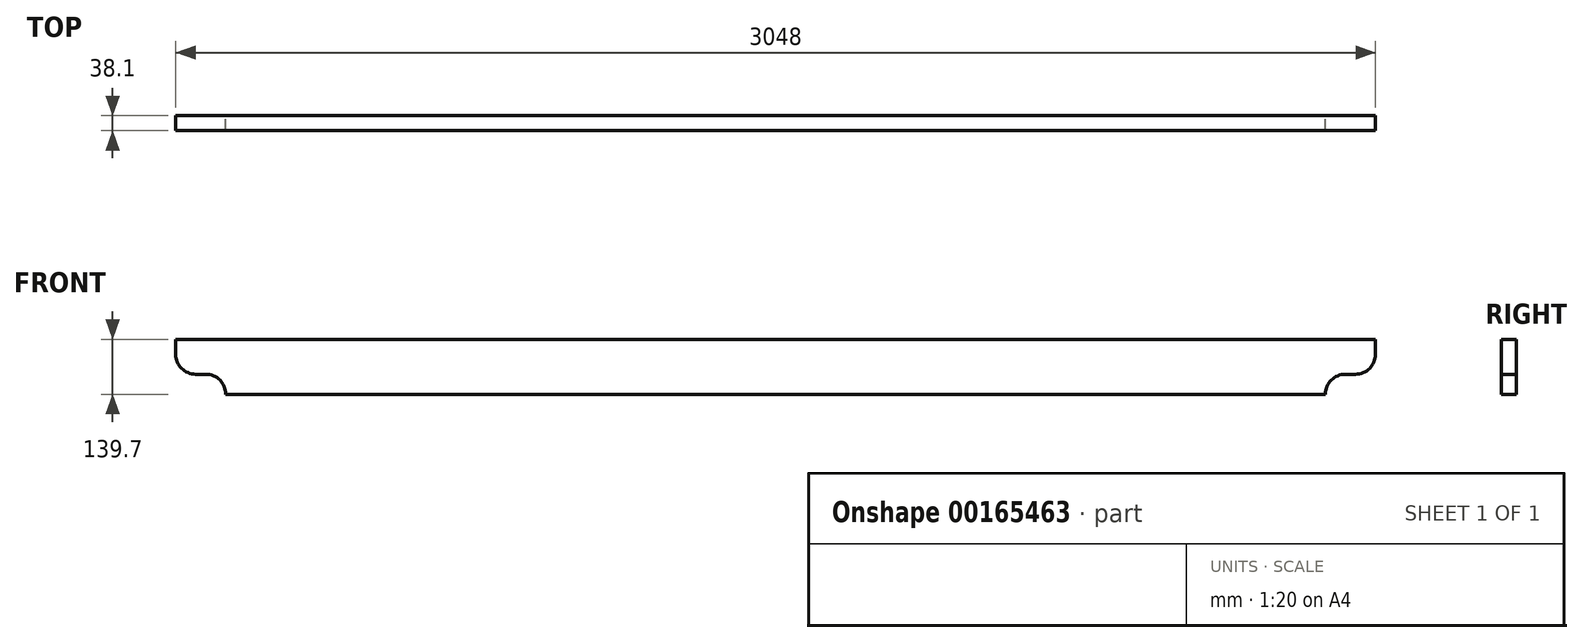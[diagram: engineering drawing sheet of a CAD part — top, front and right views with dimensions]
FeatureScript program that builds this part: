
annotation { "Feature Type Name" : "Feature", "Feature Type Description" : "" }
export const myFeature = defineFeature(function(context is Context, id is Id, definition is map)
    precondition{}
    {
        {
            var Q0;
            Q0=qCreatedBy(makeId("Front.planeOp"),FACE);
            var sketch = newSketch(context, id + "F0", { "sketchPlane" : qUnion([Q0])});
            skLineSegment(sketch, "E0.bottom", {"start": v(-1397, 0) * mm, "end": v(1397, 0) * mm});
            skLineSegment(sketch, "E0.top", {"start": v(-1524, 139.7) * mm, "end": v(1524, 139.7) * mm});
            skLineSegment(sketch, "E0.right", {"start": v(1524, 101.6) * mm, "end": v(1524, 139.7) * mm});
            skLineSegment(sketch, "E1", {"start": v(0, 0) * mm, "end": v(0, 139.7) * mm, "construction": true});
            skLineSegment(sketch, "E2", {"start": v(-1524, 139.7) * mm, "end": v(-1524, 101.6) * mm});
            skArc(sketch, "E3", {"start": v(-1524, 101.6) * mm, "mid": v(-1509.12, 65.68) * mm, "end": v(-1473.2, 50.8) * mm});
            skLineSegment(sketch, "E4", {"start": v(-1473.2, 50.8) * mm, "end": v(-1447.8, 50.8) * mm});
            skArc(sketch, "E5", {"start": v(-1447.8, 50.8) * mm, "mid": v(-1411.88, 35.92) * mm, "end": v(-1397, 0) * mm});
            skPoint(sketch, "E6.orphan", {"position": v(-1524, 0) * mm});
            skLineSegment(sketch, "E7.MirrorCS", {"start": v(1524, 139.7) * mm, "end": v(1524, 101.6) * mm});
            skPoint(sketch, "E8.MirrorP", {"position": v(1524, 0) * mm});
            skLineSegment(sketch, "E9.MirrorCS", {"start": v(1473.2, 50.8) * mm, "end": v(1447.8, 50.8) * mm});
            skArc(sketch, "E10.MirrorCS", {"start": v(1524, 101.6) * mm, "mid": v(1509.12, 65.68) * mm, "end": v(1473.2, 50.8) * mm});
            skArc(sketch, "E11.MirrorCS", {"start": v(1447.8, 50.8) * mm, "mid": v(1411.88, 35.92) * mm, "end": v(1397, 0) * mm});
            skSolve(sketch);
        }
        {
            var Q0;
            Q0=makeQuery(id+"F0.imprint","IMPRINT",FACE,{"disambiguationData":[TD([[makeQuery(id+"F0.imprint","IMPRINT",EDGE,{"derivedFrom":sQuery(id+"F0.wireOp",EDGE,"E0.bottom")}),1.0]])]});
            extrude(context, id + "F1", {"entities" : qUnion([Q0]), "endBound" : BoundingType.SYMMETRIC, "depth" : 38.1 * mm});
        }
    });
